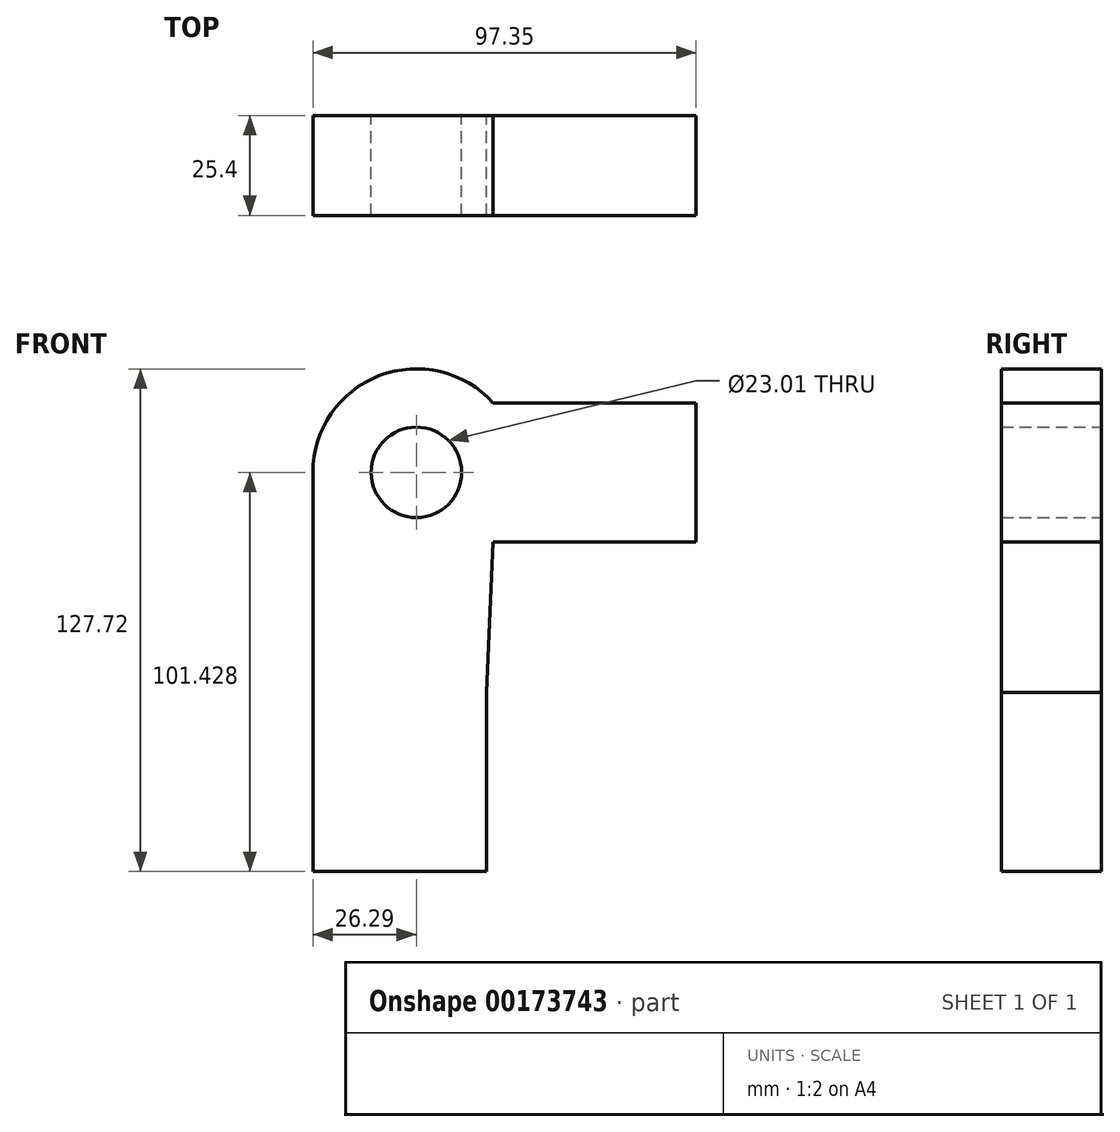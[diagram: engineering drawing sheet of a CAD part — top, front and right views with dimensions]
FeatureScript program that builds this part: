
annotation { "Feature Type Name" : "Feature", "Feature Type Description" : "" }
export const myFeature = defineFeature(function(context is Context, id is Id, definition is map)
    precondition{}
    {
        {
            var Q0;
            Q0=qCreatedBy(makeId("Front.planeOp"),FACE);
            var sketch = newSketch(context, id + "F0", { "sketchPlane" : qUnion([Q0])});
            skLineSegment(sketch, "E0.bottom", {"start": v(-39.66, -3.14) * mm, "end": v(-83.75, -3.14) * mm});
            skLineSegment(sketch, "E0.top", {"start": v(-39.66, -48.6) * mm, "end": v(-83.75, -48.6) * mm});
            skLineSegment(sketch, "E0.left", {"start": v(-39.66, -3.14) * mm, "end": v(-39.66, -48.6) * mm});
            skLineSegment(sketch, "E0.right", {"start": v(-83.75, -3.14) * mm, "end": v(-83.75, -48.6) * mm});
            skPoint(sketch, "E0.middle", {"position": v(-61.7, -25.87) * mm});
            skLineSegment(sketch, "E1.bottom", {"start": v(13.6, 35.19) * mm, "end": v(-37.96, 35.19) * mm});
            skLineSegment(sketch, "E1.top", {"start": v(13.6, 70.47) * mm, "end": v(-37.96, 70.47) * mm});
            skLineSegment(sketch, "E1.left", {"start": v(13.6, 35.19) * mm, "end": v(13.6, 70.47) * mm});
            skLineSegment(sketch, "E1.right", {"start": v(-37.96, 35.19) * mm, "end": v(-37.96, 70.47) * mm});
            skPoint(sketch, "E1.middle", {"position": v(-12.18, 52.83) * mm});
            skLineSegment(sketch, "E2.bottom", {"start": v(-83.75, 52.83) * mm, "end": v(-83.75, 52.83) * mm});
            skLineSegment(sketch, "E2.top", {"start": v(-83.75, -59.11) * mm, "end": v(-83.75, -59.11) * mm});
            skLineSegment(sketch, "E2.left", {"start": v(-83.75, 52.83) * mm, "end": v(-83.75, -59.11) * mm});
            skLineSegment(sketch, "E2.right", {"start": v(-83.75, 52.83) * mm, "end": v(-83.75, -59.11) * mm});
            skPoint(sketch, "E2.middle", {"position": v(-83.75, -3.14) * mm});
            skArc(sketch, "E3", {"start": v(-83.75, 52.83) * mm, "mid": v(-66.91, 77.36) * mm, "end": v(-37.96, 70.47) * mm});
            skLineSegment(sketch, "E4", {"start": v(-39.66, -3.14) * mm, "end": v(-37.96, 35.19) * mm});
            skCircle(sketch, "E5", {"center": v(-57.46, 52.83) * mm, "radius": 11.5 * mm});
            skSolve(sketch);
        }
        {
            var Q0;
            Q0=makeQuery(id+"F0.imprint","IMPRINT",FACE,{"disambiguationData":[TD([[makeQuery(id+"F0.imprint","IMPRINT",EDGE,{"derivedFrom":sQuery(id+"F0.wireOp",EDGE,"E1.bottom")}),-1.0]])]});
            var Q1;
            {var subQ2=sQuery(id+"F0.wireOp",EDGE,"E0.bottom");Q1=makeQuery(id+"F0.imprint","IMPRINT",FACE,{"disambiguationData":[TD([[makeQuery(id+"F0.imprint","IMPRINT",EDGE,{"derivedFrom":subQ2}),-1.0]])]});}
            var Q2;
            {var subQ0=sQuery(id+"F0.wireOp",EDGE,"E0.bottom");Q2=makeQuery(id+"F0.imprint","IMPRINT",FACE,{"disambiguationData":[TD([[makeQuery(id+"F0.imprint","IMPRINT",EDGE,{"derivedFrom":subQ0}),1.0]])]});}
            extrude(context, id + "F1", {"entities" : qUnion([Q0, Q1, Q2]), "depth" : 25.4 * mm});
        }
    });
